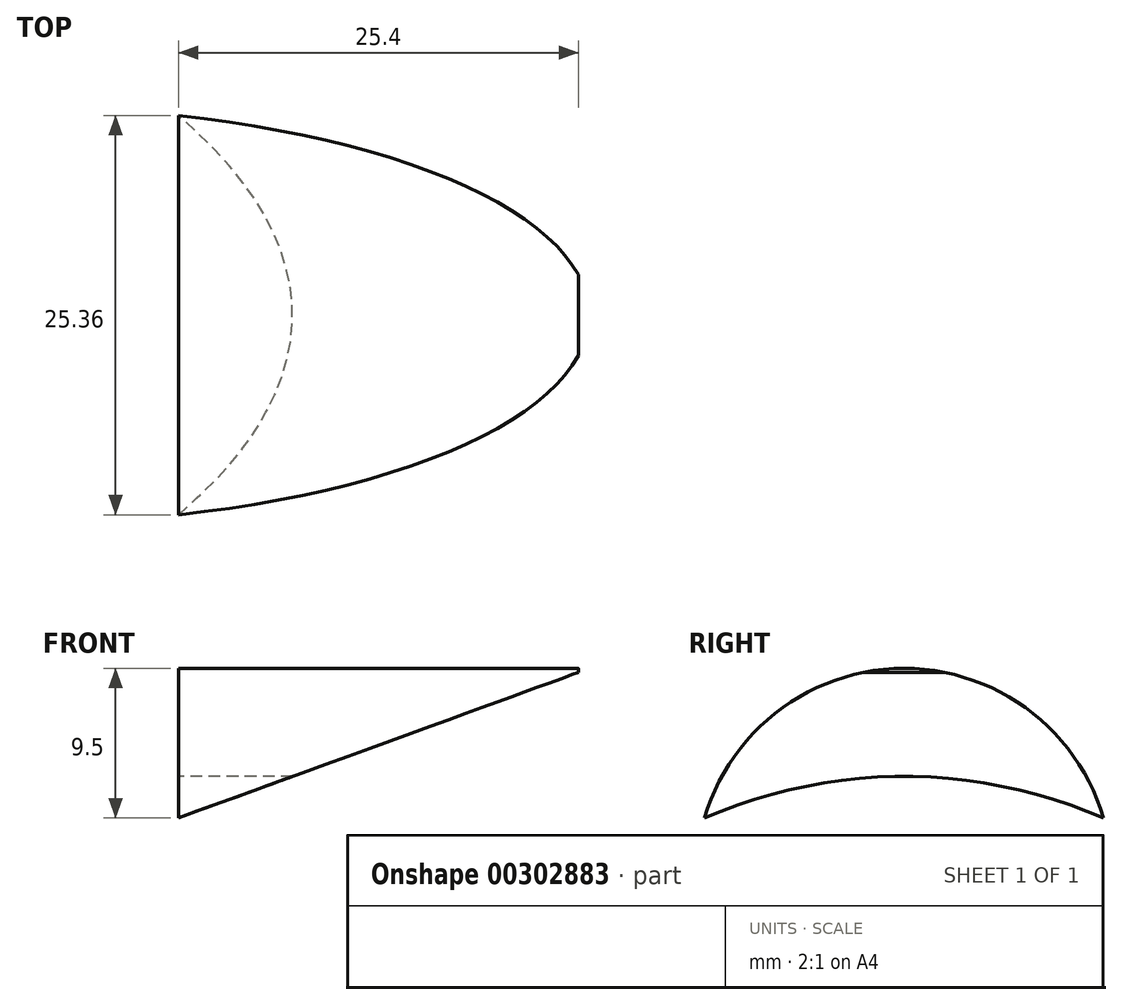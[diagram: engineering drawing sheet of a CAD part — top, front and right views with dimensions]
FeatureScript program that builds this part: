
annotation { "Feature Type Name" : "Feature", "Feature Type Description" : "" }
export const myFeature = defineFeature(function(context is Context, id is Id, definition is map)
    precondition{}
    {
        {
            var Q0;
            Q0=qCreatedBy(makeId("Right.planeOp"),FACE);
            var sketch = newSketch(context, id + "F0", { "sketchPlane" : qUnion([Q0])});
            skArc(sketch, "E0", {"start": v(12.68, 3.7) * mm, "mid": v(0, 13.2) * mm, "end": v(-12.68, 3.7) * mm});
            skArc(sketch, "E1", {"start": v(12.68, 3.7) * mm, "mid": v(0, 6.35) * mm, "end": v(-12.68, 3.7) * mm});
            skSolve(sketch);
        }
        {
            var Q0;
            Q0 = qSketchRegion(id + "F0", true);
            extrude(context, id + "F1", {"entities" : qUnion([Q0]), "depth" : 25.4 * mm});
        }
        {
            var Q0;
            Q0=qCreatedBy(makeId("Front.planeOp"),FACE);
            var sketch = newSketch(context, id + "F2", { "sketchPlane" : qUnion([Q0])});
            skLineSegment(sketch, "E2", {"start": v(25.4, 12.95) * mm, "end": v(0, 3.7) * mm});
            skLineSegment(sketch, "E3", {"start": v(0, 3.7) * mm, "end": v(25.4, 3.7) * mm});
            skLineSegment(sketch, "E4", {"start": v(25.4, 3.7) * mm, "end": v(25.4, 12.95) * mm});
            skSolve(sketch);
        }
        {
            var Q0;
            Q0 = qSketchRegion(id + "F2", true);
            extrude(context, id + "F3", {"entities" : qUnion([Q0]), "operationType" : NewBodyOperationType.REMOVE, "endBound" : BoundingType.THROUGH_ALL, "oppositeDirection" : true, "depth" : 25.4 * mm, "hasSecondDirection" : true, "secondDirectionBound" : SecondDirectionBoundingType.THROUGH_ALL, "secondDirectionOppositeDirection" : false, "secondDirectionDepth" : 25.4 * mm});
        }
    });
